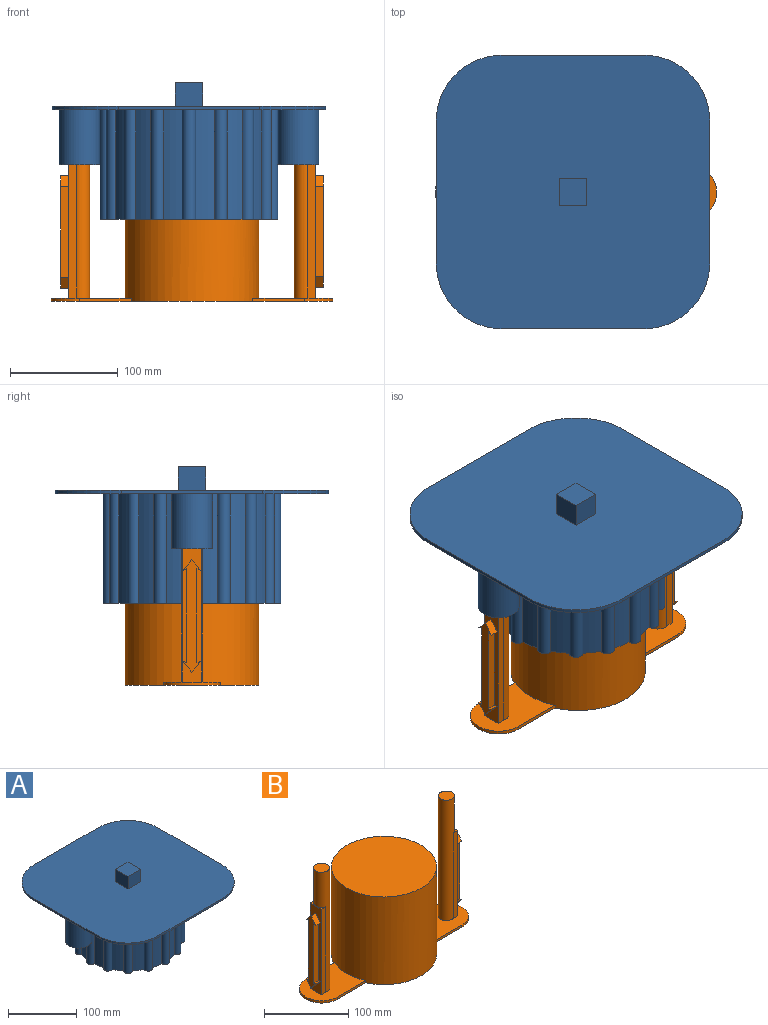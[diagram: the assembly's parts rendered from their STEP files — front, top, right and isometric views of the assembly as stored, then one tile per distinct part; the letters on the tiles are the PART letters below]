
ASSEMBLY  parts=2 mates=1
PART A: 58 faces, bbox 254x254x127 mm
  f0: plane 25.4x22.23mm, normal (0,-1,0), area 564.5mm2, adj f1,f3,f4,f9
  f1: plane 25.4x22.23mm, normal (1,0,0), area 564.5mm2, adj f0,f2,f4,f9
  f2: plane 25.4x22.23mm, normal (0,1,0), area 564.5mm2, adj f1,f3,f4,f9
  f3: plane 25.4x22.23mm, normal (-1,0,0), area 564.5mm2, adj f0,f2,f4,f9
  f4: plane 25.4x25.4mm, normal (0,0,1), area 645.2mm2, adj f0,f1,f2,f3
  f5: plane 131.36x3.18mm, normal (1,0,0), area 417.1mm2, adj f9,f10,f54,f57
  f6: plane 131.36x3.18mm, normal (0,1,0), area 417.1mm2, adj f9,f10,f54,f55
  f7: plane 131.36x3.18mm, normal (-1,0,0), area 417.1mm2, adj f9,f10,f55,f56
  f8: plane 131.36x3.18mm, normal (0,-1,0), area 417.1mm2, adj f9,f10,f56,f57
  f9: plane 254x254mm, normal (0,0,1), area 60643mm2, adj f0,f1,f2,f3,f5,f6,f7,f8
  f10: plane 254x254mm, normal (0,0,-1), area 39769.2mm2, adj f5,f6,f7,f8,f11,f12,f13,f14
  f11: cylinder r=76.2mm len=101.6mm, axis (0,0,1), area 1770.8mm2, adj f10,f12,f42,f51
  f12: cylinder r=6.25mm len=101.6mm, axis (0,0,1), area 2045.4mm2, adj f10,f11,f13,f51
  f13: cylinder r=76.2mm len=101.6mm, axis (0,0,1), area 1770.8mm2, adj f10,f12,f14,f51
  f14: cylinder r=6.25mm len=101.6mm, axis (0,0,1), area 2045.4mm2, adj f10,f13,f15,f51
  f15: cylinder r=76.2mm len=101.6mm, axis (0,0,1), area 1770.8mm2, adj f10,f14,f16,f51
  f16: cylinder r=6.25mm len=101.6mm, axis (0,0,1), area 2045.4mm2, adj f10,f15,f17,f51
  f17: cylinder r=76.2mm len=101.6mm, axis (0,0,1), area 1770.8mm2, adj f10,f16,f18,f51
  f18: cylinder r=6.25mm len=101.6mm, axis (0,0,1), area 2045.4mm2, adj f10,f17,f19,f51
  f19: cylinder r=76.2mm len=101.6mm, axis (0,0,1), area 1770.8mm2, adj f10,f18,f20,f51
  f20: cylinder r=6.25mm len=101.6mm, axis (0,0,1), area 2045.4mm2, adj f10,f19,f21,f51
  f21: cylinder r=76.2mm len=101.6mm, axis (0,0,1), area 1770.8mm2, adj f10,f20,f22,f51
  f22: cylinder r=6.25mm len=101.6mm, axis (0,0,1), area 2045.4mm2, adj f10,f21,f23,f51
  f23: cylinder r=76.2mm len=101.6mm, axis (0,0,1), area 1770.8mm2, adj f10,f22,f24,f51
  f24: cylinder r=6.25mm len=101.6mm, axis (0,0,1), area 2045.4mm2, adj f10,f23,f25,f51
  f25: cylinder r=76.2mm len=101.6mm, axis (0,0,1), area 1770.8mm2, adj f10,f24,f26,f51
  f26: cylinder r=6.25mm len=101.6mm, axis (0,0,1), area 2045.4mm2, adj f10,f25,f27,f51
  f27: cylinder r=76.2mm len=101.6mm, axis (0,0,1), area 1770.8mm2, adj f10,f26,f28,f51
  f28: cylinder r=6.25mm len=101.6mm, axis (0,0,1), area 2045.4mm2, adj f10,f27,f29,f51
  f29: cylinder r=76.2mm len=101.6mm, axis (0,0,1), area 1770.8mm2, adj f10,f28,f30,f51
  f30: cylinder r=6.25mm len=101.6mm, axis (0,0,1), area 2045.4mm2, adj f10,f29,f31,f51
  f31: cylinder r=76.2mm len=101.6mm, axis (0,0,1), area 1770.8mm2, adj f10,f30,f32,f51
  f32: cylinder r=6.25mm len=101.6mm, axis (0,0,1), area 2045.4mm2, adj f10,f31,f33,f51
  f33: cylinder r=76.2mm len=101.6mm, axis (0,0,1), area 1770.8mm2, adj f10,f32,f34,f51
  f34: cylinder r=6.25mm len=101.6mm, axis (0,0,1), area 2045.4mm2, adj f10,f33,f35,f51
  f35: cylinder r=76.2mm len=101.6mm, axis (0,0,1), area 1770.8mm2, adj f10,f34,f36,f51
  f36: cylinder r=6.25mm len=101.6mm, axis (0,0,1), area 2045.4mm2, adj f10,f35,f37,f51
  f37: cylinder r=76.2mm len=101.6mm, axis (0,0,1), area 1770.8mm2, adj f10,f36,f38,f51
  f38: cylinder r=6.25mm len=101.6mm, axis (0,0,1), area 2045.4mm2, adj f10,f37,f39,f51
  f39: cylinder r=76.2mm len=101.6mm, axis (0,0,1), area 1770.8mm2, adj f10,f38,f40,f51
  f40: cylinder r=6.25mm len=101.6mm, axis (0,0,1), area 2045.4mm2, adj f10,f39,f41,f51
  f41: cylinder r=76.2mm len=101.6mm, axis (0,0,1), area 1770.8mm2, adj f10,f40,f42,f51
  f42: cylinder r=6.25mm len=101.6mm, axis (0,0,1), area 2045.4mm2, adj f10,f11,f41,f51
  f43: cylinder r=9.53mm len=50.8mm, axis (0,0,1), area 3040.2mm2, adj f45,f46
  f44: cylinder r=19.05mm len=50.8mm, axis (0,0,1), area 6080.5mm2, adj f10,f45
  f45: plane 38.1x38.1mm, normal (0,0,-1), area 855.1mm2, adj f43,f44
  f46: plane 19.05x19.05mm, normal (0,0,-1), area 285mm2, adj f43
  f47: cylinder r=19.05mm len=50.8mm, axis (0,0,1), area 6080.5mm2, adj f10,f49
  f48: cylinder r=9.53mm len=50.8mm, axis (0,0,1), area 3040.2mm2, adj f49,f50
  f49: plane 38.1x38.1mm, normal (0,0,-1), area 855.1mm2, adj f47,f48
  f50: plane 19.05x19.05mm, normal (0,0,-1), area 285mm2, adj f48
  f51: plane 164.89x164.89mm, normal (0,0,-1), area 6571.1mm2, adj f11,f12,f13,f14,f15,f16,f17,f18
  f52: plane 127x127mm, normal (0,0,-1), area 12667.7mm2, adj f53
  f53: cylinder r=63.5mm len=127mm, axis (0,0,1), area 40536.6mm2, adj f51,f52
  f54: cylinder r=61.32mm len=61.32mm, axis (0,0,1), area 305.8mm2, adj f5,f6,f9,f10
  f55: cylinder r=61.32mm len=61.32mm, axis (0,0,-1), area 305.8mm2, adj f6,f7,f9,f10
  f56: cylinder r=61.32mm len=61.32mm, axis (0,0,1), area 305.8mm2, adj f7,f8,f9,f10
  f57: cylinder r=61.32mm len=61.32mm, axis (0,0,-1), area 305.8mm2, adj f5,f8,f9,f10
PART B: 49 faces, bbox 261.1x124.5x177.8 mm
  f0: plane 123.83x18.3mm, normal (-1,0,0), area 1344.6mm2, adj f4,f20,f21,f22,f38,f39,f40,f41
  f1: cylinder r=9.53mm len=174.63mm, axis (0,0,-1), area 7412mm2, adj f2,f10,f23,f25,f26
  f2: plane 74.06x52.22mm, normal (0,0,1), area 3048mm2, adj f1,f11,f12,f13,f14,f23,f24,f25
  f3: cylinder r=9.53mm len=174.63mm, axis (0,0,-1), area 7412mm2, adj f4,f6,f20,f21,f22
  f4: plane 74.06x52.22mm, normal (0,0,1), area 3048mm2, adj f0,f3,f7,f8,f9,f14,f20,f21
  f5: plane 261.1x124.46mm, normal (0,0,-1), area 18342.4mm2, adj f7,f8,f9,f11,f12,f13,f14,f16
  f6: plane 19.05x19.05mm, normal (0,0,1), area 285mm2, adj f3
  f7: plane 47.95x3.18mm, normal (0,1,0), area 152.3mm2, adj f4,f5,f8,f14
  f8: cylinder r=26.11mm len=52.22mm, axis (0,0,-1), area 260.4mm2, adj f4,f5,f7,f9
  f9: plane 47.95x3.18mm, normal (0,-1,0), area 152.3mm2, adj f4,f5,f8,f14
  f10: plane 19.05x19.05mm, normal (0,0,1), area 285mm2, adj f1
  f11: cylinder r=26.11mm len=52.22mm, axis (0,0,-1), area 260.4mm2, adj f2,f5,f12,f13
  f12: plane 47.95x3.18mm, normal (0,1,0), area 152.3mm2, adj f2,f5,f11,f14
  f13: plane 47.95x3.18mm, normal (0,-1,0), area 152.3mm2, adj f2,f5,f11,f14
  f14: cylinder r=62.23mm len=127mm, axis (0,0,-1), area 49315.1mm2, adj f2,f4,f5,f7,f9,f12,f13,f15
  f15: plane 124.46x124.46mm, normal (0,0,1), area 12166mm2, adj f14
  f16: cylinder r=9.53mm len=25.4mm, axis (0,0,-1), area 1520.1mm2, adj f5,f17
  f17: plane 19.05x19.05mm, normal (0,0,-1), area 285mm2, adj f16
  f18: cylinder r=9.53mm len=25.4mm, axis (0,0,-1), area 1520.1mm2, adj f5,f19
  f19: plane 19.05x19.05mm, normal (0,0,-1), area 285mm2, adj f18
  f20: plane 123.83x7.26mm, normal (0,1,0), area 898.3mm2, adj f0,f3,f4,f22
  f21: plane 123.83x7.26mm, normal (0,-1,0), area 898.3mm2, adj f0,f3,f4,f22
  f22: plane 18.3x7.26mm, normal (0,0,1), area 40.1mm2, adj f0,f3,f20,f21
  f23: plane 123.83x7.26mm, normal (0,-1,0), area 898.3mm2, adj f1,f2,f24,f26
  f24: plane 123.83x18.3mm, normal (1,0,0), area 1352.4mm2, adj f2,f23,f25,f26,f27,f28,f29,f30
  f25: plane 123.83x7.26mm, normal (0,1,0), area 898.3mm2, adj f1,f2,f24,f26
  f26: plane 18.3x7.26mm, normal (0,0,1), area 40.1mm2, adj f1,f23,f24,f25
  f27: plane 87.6x7.62mm, normal (0,-1,0), area 667.5mm2, adj f24,f28,f36,f37
  f28: plane 7.62x3.65mm, normal (0,0.46,0.89), area 31.2mm2, adj f24,f27,f29,f37
  f29: plane 10.01x8.19mm, normal (0,-0.77,-0.63), area 98.5mm2, adj f24,f28,f30,f37
  f30: plane 10.01x8.19mm, normal (0,0.77,-0.63), area 98.5mm2, adj f24,f29,f31,f37
  f31: plane 7.62x3.65mm, normal (0,-0.46,0.89), area 31.2mm2, adj f24,f30,f32,f37
  f32: plane 87.6x7.62mm, normal (0,1,0), area 667.5mm2, adj f24,f31,f33,f37
  f33: plane 7.62x3.65mm, normal (0,-0.46,-0.89), area 31.2mm2, adj f24,f32,f34,f37
  f34: plane 10.01x8.19mm, normal (0,0.77,0.63), area 98.5mm2, adj f24,f33,f35,f37
  f35: plane 10.01x8.19mm, normal (0,-0.77,0.63), area 98.5mm2, adj f24,f34,f36,f37
  f36: plane 7.62x3.65mm, normal (0,0.46,-0.89), area 31.2mm2, adj f24,f27,f35,f37
  f37: plane 103.88x16.39mm, normal (1,0,0), area 913mm2, adj f27,f28,f29,f30,f31,f32,f33,f34
  f38: plane 87.25x7.62mm, normal (0,-1,0), area 664.8mm2, adj f0,f39,f47,f48
  f39: plane 7.62x3.65mm, normal (0,0.46,-0.89), area 31.2mm2, adj f0,f38,f40,f48
  f40: plane 10.01x8.19mm, normal (0,-0.77,0.63), area 98.5mm2, adj f0,f39,f41,f48
  f41: plane 10.01x8.19mm, normal (0,0.77,0.63), area 98.5mm2, adj f0,f40,f42,f48
  f42: plane 7.62x3.65mm, normal (0,-0.46,-0.89), area 31.2mm2, adj f0,f41,f43,f48
  f43: plane 87.25x7.62mm, normal (0,1,0), area 664.8mm2, adj f0,f42,f44,f48
  f44: plane 7.62x3.65mm, normal (0,-0.27,0.96), area 28.8mm2, adj f0,f43,f45,f48
  f45: plane 10.01x8.19mm, normal (0,0.77,-0.63), area 98.5mm2, adj f0,f44,f46,f48
  f46: plane 10.01x8.19mm, normal (0,-0.77,-0.63), area 98.5mm2, adj f0,f45,f47,f48
  f47: plane 7.62x3.65mm, normal (0,0.27,0.96), area 28.8mm2, adj f0,f38,f46,f48
  f48: plane 104.39x16.39mm, normal (-1,0,0), area 920.7mm2, adj f38,f39,f40,f41,f42,f43,f44,f45
PLACE A t=(-260.04,110.36,-26.09)mm
PLACE B t=(-257.2,110.36,-203.89)mm
MATE slider B.f3 <-> A.f44  axis (0,0,-1) through (-361.64,110.36,-26.09)mm
